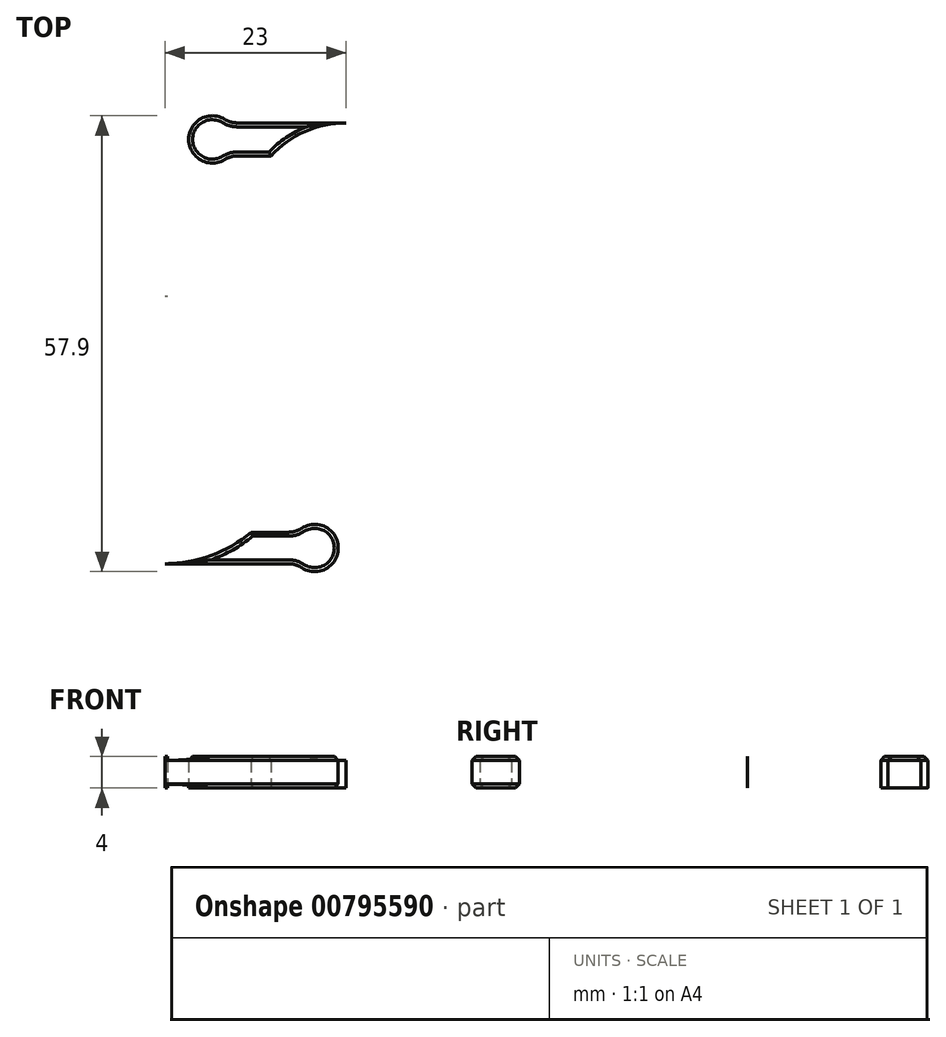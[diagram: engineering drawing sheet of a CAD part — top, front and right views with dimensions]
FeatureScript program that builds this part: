
annotation { "Feature Type Name" : "Feature", "Feature Type Description" : "" }
export const myFeature = defineFeature(function(context is Context, id is Id, definition is map)
    precondition{}
    {
        {
            var Q0;
            Q0=qCreatedBy(makeId("Top.planeOp"),FACE);
            var sketch = newSketch(context, id + "F0", { "sketchPlane" : qUnion([Q0])});
            skCircle(sketch, "E0", {"center": v(0, 0) * mm, "radius": 17 * mm});
            skCircle(sketch, "E1", {"center": v(0, 0) * mm, "radius": 13 * mm});
            skCircle(sketch, "E2", {"center": v(23, 26) * mm, "radius": 13 * mm});
            skCircle(sketch, "E3", {"center": v(23, 25.8) * mm, "radius": 9 * mm});
            skLineSegment(sketch, "E4", {"start": v(0, 17) * mm, "end": v(23, 16.8) * mm});
            skLineSegment(sketch, "E5", {"start": v(0, 13) * mm, "end": v(23, 13) * mm});
            skLineSegment(sketch, "E6", {"start": v(0, -13) * mm, "end": v(19, -13) * mm});
            skLineSegment(sketch, "E7", {"start": v(0, -17) * mm, "end": v(19, -17) * mm});
            skLineSegment(sketch, "E8", {"start": v(23, 39) * mm, "end": v(6, 39) * mm});
            skLineSegment(sketch, "E9", {"start": v(23, 34.8) * mm, "end": v(6, 34.8) * mm});
            skLineSegment(sketch, "E10", {"start": v(6, 39) * mm, "end": v(6, 34.8) * mm});
            skLineSegment(sketch, "E11", {"start": v(19, -13) * mm, "end": v(19, -17) * mm});
            skCircle(sketch, "E12", {"center": v(6, 36.9) * mm, "radius": 3 * mm});
            skCircle(sketch, "E13", {"center": v(19, -15) * mm, "radius": 3 * mm});
            skSolve(sketch);
        }
        {
            var Q0;
            {var subQ0=sQuery(id+"F0.wireOp",EDGE,"E10");Q0=makeQuery(id+"F0.imprint","IMPRINT",FACE,{"disambiguationData":[TD([[makeQuery(id+"F0.imprint","IMPRINT",EDGE,{"derivedFrom":subQ0}),-1.0]])]});}
            var Q1;
            {var subQ5=sQuery(id+"F0.wireOp",EDGE,"E3");var subQ7=makeQuery(id+"F0.imprint","IMPRINT",VERTEX,{"derivedFrom":subQ5});Q1=makeQuery(id+"F0.imprint","IMPRINT",FACE,{"disambiguationData":[TD([[makeQuery(id+"F0.imprint","IMPRINT",EDGE,{"disambiguationData":[TD([[subQ7,1.0]])],"derivedFrom":subQ5}),-1.0]])]});}
            var Q2;
            {var subQ0=sQuery(id+"F0.wireOp",EDGE,"E0");var subQ4=sQuery(id+"F0.wireOp",EDGE,"E4");var subQ6=makeQuery(id+"F0.imprint","INTERSECT",VERTEX,{"disambiguationData":[OD(1.0)],"derivedFrom":[subQ0,subQ4]});Q2=makeQuery(id+"F0.imprint","IMPRINT",FACE,{"disambiguationData":[TD([[makeQuery(id+"F0.imprint","IMPRINT",EDGE,{"disambiguationData":[TD([[subQ6,1.0]])],"derivedFrom":subQ0}),1.0]])]});}
            var Q3;
            {var subQ0=sQuery(id+"F0.wireOp",EDGE,"E8");var subQ1=sQuery(id+"F0.wireOp",EDGE,"E2");var subQ2=makeQuery(id+"F0.imprint","INTERSECT",VERTEX,{"derivedFrom":[subQ1,subQ0]});Q3=makeQuery(id+"F0.imprint","IMPRINT",FACE,{"disambiguationData":[TD([[makeQuery(id+"F0.imprint","IMPRINT",EDGE,{"disambiguationData":[TD([[subQ2,-1.0]])],"derivedFrom":subQ1}),-1.0]])]});}
            var Q4;
            {var subQ0=sQuery(id+"F0.wireOp",EDGE,"E4");var subQ1=sQuery(id+"F0.wireOp",EDGE,"E0");var subQ2=makeQuery(id+"F0.imprint","INTERSECT",VERTEX,{"disambiguationData":[OD(1.0)],"derivedFrom":[subQ1,subQ0]});Q4=makeQuery(id+"F0.imprint","IMPRINT",FACE,{"disambiguationData":[TD([[makeQuery(id+"F0.imprint","IMPRINT",EDGE,{"disambiguationData":[TD([[subQ2,1.0]])],"derivedFrom":subQ1}),-1.0]])]});}
            var Q5;
            {var subQ0=sQuery(id+"F0.wireOp",EDGE,"E7");var subQ1=sQuery(id+"F0.wireOp",EDGE,"E0");var subQ2=makeQuery(id+"F0.imprint","INTERSECT",VERTEX,{"derivedFrom":[subQ1,subQ0]});Q5=makeQuery(id+"F0.imprint","IMPRINT",FACE,{"disambiguationData":[TD([[makeQuery(id+"F0.imprint","IMPRINT",EDGE,{"disambiguationData":[TD([[subQ2,-1.0]])],"derivedFrom":subQ1}),-1.0]])]});}
            var Q6;
            {var subQ0=sQuery(id+"F0.wireOp",EDGE,"E11");Q6=makeQuery(id+"F0.imprint","IMPRINT",FACE,{"disambiguationData":[TD([[makeQuery(id+"F0.imprint","IMPRINT",EDGE,{"derivedFrom":subQ0}),-1.0]])]});}
            var Q7;
            {var subQ0=sQuery(id+"F0.wireOp",EDGE,"E10");Q7=makeQuery(id+"F0.imprint","IMPRINT",FACE,{"disambiguationData":[TD([[makeQuery(id+"F0.imprint","IMPRINT",EDGE,{"derivedFrom":subQ0}),1.0]])]});}
            var Q8;
            {var subQ0=sQuery(id+"F0.wireOp",EDGE,"E11");Q8=makeQuery(id+"F0.imprint","IMPRINT",FACE,{"disambiguationData":[TD([[makeQuery(id+"F0.imprint","IMPRINT",EDGE,{"derivedFrom":subQ0}),1.0]])]});}
            extrude(context, id + "F1", {"entities" : qUnion([Q0, Q1, Q2, Q3, Q4, Q5, Q6, Q7, Q8]), "depth" : 4 * mm, "offsetDistance" : 25 * mm});
        }
        {
            var Q0;
            Q0=makeQuery(id+"F1.opExtrude","SWEPT_EDGE",EDGE,{"disambiguationData":[OSD([sQuery(id+"F0.wireOp",EDGE,"E7"),sQuery(id+"F0.wireOp",EDGE,"E13")])]});
            var Q1;
            Q1=makeQuery(id+"F1.opExtrude","SWEPT_EDGE",EDGE,{"disambiguationData":[OSD([sQuery(id+"F0.wireOp",EDGE,"E9"),sQuery(id+"F0.wireOp",EDGE,"E12")])]});
            var Q2;
            Q2=makeQuery(id+"F1.opExtrude","SWEPT_EDGE",EDGE,{"disambiguationData":[OSD([sQuery(id+"F0.wireOp",EDGE,"E6"),sQuery(id+"F0.wireOp",EDGE,"E13")])]});
            var Q3;
            Q3=makeQuery(id+"F1.opExtrude","SWEPT_EDGE",EDGE,{"disambiguationData":[OSD([sQuery(id+"F0.wireOp",EDGE,"E8"),sQuery(id+"F0.wireOp",EDGE,"E12")])]});
            fillet(context, id + "F2", {"entities" : qUnion([Q0, Q1, Q2, Q3]), "radius" : 3 * mm, "tangentPropagation" : true, "allowEdgeOverflow" : false});
        }
        {
            var Q0;
            Q0=makeQuery(id+"F1.opExtrude","CAP_EDGE",EDGE,{"disambiguationData":[OSD([sQuery(id+"F0.wireOp",EDGE,"E7")])],"isStart":false});
            var Q1;
            Q1=makeQuery(id+"F1.opExtrude","CAP_EDGE",EDGE,{"disambiguationData":[OSD([sQuery(id+"F0.wireOp",EDGE,"E6")])],"isStart":false});
            var Q2;
            Q2=makeQuery(id+"F1.opExtrude","CAP_EDGE",EDGE,{"disambiguationData":[OSD([sQuery(id+"F0.wireOp",EDGE,"E1")])],"isStart":false});
            var Q3;
            Q3=makeQuery(id+"F1.opExtrude","CAP_EDGE",EDGE,{"disambiguationData":[OSD([sQuery(id+"F0.wireOp",EDGE,"E0")])],"isStart":false});
            var Q4;
            Q4=makeQuery(id+"F1.opExtrude","CAP_EDGE",EDGE,{"disambiguationData":[OSD([sQuery(id+"F0.wireOp",EDGE,"E5")])],"isStart":false});
            var Q5;
            Q5=makeQuery(id+"F1.opExtrude","CAP_EDGE",EDGE,{"disambiguationData":[OSD([sQuery(id+"F0.wireOp",EDGE,"E4")])],"isStart":false});
            var Q6;
            Q6=makeQuery(id+"F1.opExtrude","CAP_EDGE",EDGE,{"disambiguationData":[OSD([sQuery(id+"F0.wireOp",EDGE,"E13")])],"isStart":false});
            var Q7;
            {var subQ0=sQuery(id+"F0.wireOp",EDGE,"E13");var subQ1=sQuery(id+"F0.wireOp",EDGE,"E6");Q7=makeQuery(id+"F2.opFillet","BLEND_EDGE",EDGE,{"blendedFrom":[makeQuery(id+"F1.opExtrude","SWEPT_EDGE",EDGE,{"disambiguationData":[OSD([subQ1,subQ0])]}),makeQuery(id+"F1.opExtrude","CAP_FACE",FACE,{"disambiguationData":[OSD([sQuery(id+"F0.wireOp",EDGE,"E0"),sQuery(id+"F0.wireOp",EDGE,"E1"),sQuery(id+"F0.wireOp",EDGE,"E2"),sQuery(id+"F0.wireOp",EDGE,"E3"),sQuery(id+"F0.wireOp",EDGE,"E4"),sQuery(id+"F0.wireOp",EDGE,"E5"),subQ1,sQuery(id+"F0.wireOp",EDGE,"E7"),sQuery(id+"F0.wireOp",EDGE,"E8"),sQuery(id+"F0.wireOp",EDGE,"E9"),sQuery(id+"F0.wireOp",EDGE,"E12"),subQ0])],"isStart":false})],"blendedInto":[makeQuery(id+"F1.opExtrude","CAP_FACE",FACE,{"disambiguationData":[OSD([sQuery(id+"F0.wireOp",EDGE,"E0"),sQuery(id+"F0.wireOp",EDGE,"E1"),sQuery(id+"F0.wireOp",EDGE,"E2"),sQuery(id+"F0.wireOp",EDGE,"E3"),sQuery(id+"F0.wireOp",EDGE,"E4"),sQuery(id+"F0.wireOp",EDGE,"E5"),subQ1,sQuery(id+"F0.wireOp",EDGE,"E7"),sQuery(id+"F0.wireOp",EDGE,"E8"),sQuery(id+"F0.wireOp",EDGE,"E9"),sQuery(id+"F0.wireOp",EDGE,"E12"),subQ0])],"isStart":false})]});}
            var Q8;
            {var subQ0=sQuery(id+"F0.wireOp",EDGE,"E13");var subQ1=sQuery(id+"F0.wireOp",EDGE,"E7");Q8=makeQuery(id+"F2.opFillet","BLEND_EDGE",EDGE,{"blendedFrom":[makeQuery(id+"F1.opExtrude","SWEPT_EDGE",EDGE,{"disambiguationData":[OSD([subQ1,subQ0])]}),makeQuery(id+"F1.opExtrude","CAP_FACE",FACE,{"disambiguationData":[OSD([sQuery(id+"F0.wireOp",EDGE,"E0"),sQuery(id+"F0.wireOp",EDGE,"E1"),sQuery(id+"F0.wireOp",EDGE,"E2"),sQuery(id+"F0.wireOp",EDGE,"E3"),sQuery(id+"F0.wireOp",EDGE,"E4"),sQuery(id+"F0.wireOp",EDGE,"E5"),sQuery(id+"F0.wireOp",EDGE,"E6"),subQ1,sQuery(id+"F0.wireOp",EDGE,"E8"),sQuery(id+"F0.wireOp",EDGE,"E9"),sQuery(id+"F0.wireOp",EDGE,"E12"),subQ0])],"isStart":false})],"blendedInto":[makeQuery(id+"F1.opExtrude","CAP_FACE",FACE,{"disambiguationData":[OSD([sQuery(id+"F0.wireOp",EDGE,"E0"),sQuery(id+"F0.wireOp",EDGE,"E1"),sQuery(id+"F0.wireOp",EDGE,"E2"),sQuery(id+"F0.wireOp",EDGE,"E3"),sQuery(id+"F0.wireOp",EDGE,"E4"),sQuery(id+"F0.wireOp",EDGE,"E5"),sQuery(id+"F0.wireOp",EDGE,"E6"),subQ1,sQuery(id+"F0.wireOp",EDGE,"E8"),sQuery(id+"F0.wireOp",EDGE,"E9"),sQuery(id+"F0.wireOp",EDGE,"E12"),subQ0])],"isStart":false})]});}
            var Q9;
            Q9=makeQuery(id+"F1.opExtrude","CAP_EDGE",EDGE,{"disambiguationData":[OSD([sQuery(id+"F0.wireOp",EDGE,"E2")])],"isStart":false});
            var Q10;
            Q10=makeQuery(id+"F1.opExtrude","CAP_EDGE",EDGE,{"disambiguationData":[OSD([sQuery(id+"F0.wireOp",EDGE,"E3")])],"isStart":false});
            var Q11;
            Q11=makeQuery(id+"F1.opExtrude","CAP_EDGE",EDGE,{"disambiguationData":[OSD([sQuery(id+"F0.wireOp",EDGE,"E9")])],"isStart":false});
            var Q12;
            Q12=makeQuery(id+"F1.opExtrude","CAP_EDGE",EDGE,{"disambiguationData":[OSD([sQuery(id+"F0.wireOp",EDGE,"E8")])],"isStart":false});
            var Q13;
            {var subQ0=sQuery(id+"F0.wireOp",EDGE,"E12");var subQ1=sQuery(id+"F0.wireOp",EDGE,"E9");Q13=makeQuery(id+"F2.opFillet","BLEND_EDGE",EDGE,{"blendedFrom":[makeQuery(id+"F1.opExtrude","SWEPT_EDGE",EDGE,{"disambiguationData":[OSD([subQ1,subQ0])]}),makeQuery(id+"F1.opExtrude","CAP_FACE",FACE,{"disambiguationData":[OSD([sQuery(id+"F0.wireOp",EDGE,"E0"),sQuery(id+"F0.wireOp",EDGE,"E1"),sQuery(id+"F0.wireOp",EDGE,"E2"),sQuery(id+"F0.wireOp",EDGE,"E3"),sQuery(id+"F0.wireOp",EDGE,"E4"),sQuery(id+"F0.wireOp",EDGE,"E5"),sQuery(id+"F0.wireOp",EDGE,"E6"),sQuery(id+"F0.wireOp",EDGE,"E7"),sQuery(id+"F0.wireOp",EDGE,"E8"),subQ1,subQ0,sQuery(id+"F0.wireOp",EDGE,"E13")])],"isStart":false})],"blendedInto":[makeQuery(id+"F1.opExtrude","CAP_FACE",FACE,{"disambiguationData":[OSD([sQuery(id+"F0.wireOp",EDGE,"E0"),sQuery(id+"F0.wireOp",EDGE,"E1"),sQuery(id+"F0.wireOp",EDGE,"E2"),sQuery(id+"F0.wireOp",EDGE,"E3"),sQuery(id+"F0.wireOp",EDGE,"E4"),sQuery(id+"F0.wireOp",EDGE,"E5"),sQuery(id+"F0.wireOp",EDGE,"E6"),sQuery(id+"F0.wireOp",EDGE,"E7"),sQuery(id+"F0.wireOp",EDGE,"E8"),subQ1,subQ0,sQuery(id+"F0.wireOp",EDGE,"E13")])],"isStart":false})]});}
            var Q14;
            {var subQ0=sQuery(id+"F0.wireOp",EDGE,"E12");var subQ1=sQuery(id+"F0.wireOp",EDGE,"E8");Q14=makeQuery(id+"F2.opFillet","BLEND_EDGE",EDGE,{"blendedFrom":[makeQuery(id+"F1.opExtrude","SWEPT_EDGE",EDGE,{"disambiguationData":[OSD([subQ1,subQ0])]}),makeQuery(id+"F1.opExtrude","CAP_FACE",FACE,{"disambiguationData":[OSD([sQuery(id+"F0.wireOp",EDGE,"E0"),sQuery(id+"F0.wireOp",EDGE,"E1"),sQuery(id+"F0.wireOp",EDGE,"E2"),sQuery(id+"F0.wireOp",EDGE,"E3"),sQuery(id+"F0.wireOp",EDGE,"E4"),sQuery(id+"F0.wireOp",EDGE,"E5"),sQuery(id+"F0.wireOp",EDGE,"E6"),sQuery(id+"F0.wireOp",EDGE,"E7"),subQ1,sQuery(id+"F0.wireOp",EDGE,"E9"),subQ0,sQuery(id+"F0.wireOp",EDGE,"E13")])],"isStart":false})],"blendedInto":[makeQuery(id+"F1.opExtrude","CAP_FACE",FACE,{"disambiguationData":[OSD([sQuery(id+"F0.wireOp",EDGE,"E0"),sQuery(id+"F0.wireOp",EDGE,"E1"),sQuery(id+"F0.wireOp",EDGE,"E2"),sQuery(id+"F0.wireOp",EDGE,"E3"),sQuery(id+"F0.wireOp",EDGE,"E4"),sQuery(id+"F0.wireOp",EDGE,"E5"),sQuery(id+"F0.wireOp",EDGE,"E6"),sQuery(id+"F0.wireOp",EDGE,"E7"),subQ1,sQuery(id+"F0.wireOp",EDGE,"E9"),subQ0,sQuery(id+"F0.wireOp",EDGE,"E13")])],"isStart":false})]});}
            var Q15;
            Q15=makeQuery(id+"F1.opExtrude","CAP_EDGE",EDGE,{"disambiguationData":[OSD([sQuery(id+"F0.wireOp",EDGE,"E12")])],"isStart":false});
            var Q16;
            Q16=makeQuery(id+"F1.opExtrude","CAP_EDGE",EDGE,{"disambiguationData":[OSD([sQuery(id+"F0.wireOp",EDGE,"E13")])],"isStart":true});
            var Q17;
            {var subQ0=sQuery(id+"F0.wireOp",EDGE,"E13");var subQ1=sQuery(id+"F0.wireOp",EDGE,"E7");Q17=makeQuery(id+"F2.opFillet","BLEND_EDGE",EDGE,{"blendedFrom":[makeQuery(id+"F1.opExtrude","SWEPT_EDGE",EDGE,{"disambiguationData":[OSD([subQ1,subQ0])]}),makeQuery(id+"F1.opExtrude","CAP_FACE",FACE,{"disambiguationData":[OSD([sQuery(id+"F0.wireOp",EDGE,"E0"),sQuery(id+"F0.wireOp",EDGE,"E1"),sQuery(id+"F0.wireOp",EDGE,"E2"),sQuery(id+"F0.wireOp",EDGE,"E3"),sQuery(id+"F0.wireOp",EDGE,"E4"),sQuery(id+"F0.wireOp",EDGE,"E5"),sQuery(id+"F0.wireOp",EDGE,"E6"),subQ1,sQuery(id+"F0.wireOp",EDGE,"E8"),sQuery(id+"F0.wireOp",EDGE,"E9"),sQuery(id+"F0.wireOp",EDGE,"E12"),subQ0])],"isStart":true})],"blendedInto":[makeQuery(id+"F1.opExtrude","CAP_FACE",FACE,{"disambiguationData":[OSD([sQuery(id+"F0.wireOp",EDGE,"E0"),sQuery(id+"F0.wireOp",EDGE,"E1"),sQuery(id+"F0.wireOp",EDGE,"E2"),sQuery(id+"F0.wireOp",EDGE,"E3"),sQuery(id+"F0.wireOp",EDGE,"E4"),sQuery(id+"F0.wireOp",EDGE,"E5"),sQuery(id+"F0.wireOp",EDGE,"E6"),subQ1,sQuery(id+"F0.wireOp",EDGE,"E8"),sQuery(id+"F0.wireOp",EDGE,"E9"),sQuery(id+"F0.wireOp",EDGE,"E12"),subQ0])],"isStart":true})]});}
            var Q18;
            Q18=makeQuery(id+"F1.opExtrude","CAP_EDGE",EDGE,{"disambiguationData":[OSD([sQuery(id+"F0.wireOp",EDGE,"E6")])],"isStart":true});
            var Q19;
            Q19=makeQuery(id+"F1.opExtrude","CAP_EDGE",EDGE,{"disambiguationData":[OSD([sQuery(id+"F0.wireOp",EDGE,"E7")])],"isStart":true});
            var Q20;
            {var subQ0=sQuery(id+"F0.wireOp",EDGE,"E13");var subQ1=sQuery(id+"F0.wireOp",EDGE,"E6");Q20=makeQuery(id+"F2.opFillet","BLEND_EDGE",EDGE,{"blendedFrom":[makeQuery(id+"F1.opExtrude","SWEPT_EDGE",EDGE,{"disambiguationData":[OSD([subQ1,subQ0])]}),makeQuery(id+"F1.opExtrude","CAP_FACE",FACE,{"disambiguationData":[OSD([sQuery(id+"F0.wireOp",EDGE,"E0"),sQuery(id+"F0.wireOp",EDGE,"E1"),sQuery(id+"F0.wireOp",EDGE,"E2"),sQuery(id+"F0.wireOp",EDGE,"E3"),sQuery(id+"F0.wireOp",EDGE,"E4"),sQuery(id+"F0.wireOp",EDGE,"E5"),subQ1,sQuery(id+"F0.wireOp",EDGE,"E7"),sQuery(id+"F0.wireOp",EDGE,"E8"),sQuery(id+"F0.wireOp",EDGE,"E9"),sQuery(id+"F0.wireOp",EDGE,"E12"),subQ0])],"isStart":true})],"blendedInto":[makeQuery(id+"F1.opExtrude","CAP_FACE",FACE,{"disambiguationData":[OSD([sQuery(id+"F0.wireOp",EDGE,"E0"),sQuery(id+"F0.wireOp",EDGE,"E1"),sQuery(id+"F0.wireOp",EDGE,"E2"),sQuery(id+"F0.wireOp",EDGE,"E3"),sQuery(id+"F0.wireOp",EDGE,"E4"),sQuery(id+"F0.wireOp",EDGE,"E5"),subQ1,sQuery(id+"F0.wireOp",EDGE,"E7"),sQuery(id+"F0.wireOp",EDGE,"E8"),sQuery(id+"F0.wireOp",EDGE,"E9"),sQuery(id+"F0.wireOp",EDGE,"E12"),subQ0])],"isStart":true})]});}
            var Q21;
            Q21=makeQuery(id+"F1.opExtrude","CAP_EDGE",EDGE,{"disambiguationData":[OSD([sQuery(id+"F0.wireOp",EDGE,"E1")])],"isStart":true});
            var Q22;
            Q22=makeQuery(id+"F1.opExtrude","CAP_EDGE",EDGE,{"disambiguationData":[OSD([sQuery(id+"F0.wireOp",EDGE,"E0")])],"isStart":true});
            var Q23;
            Q23=makeQuery(id+"F1.opExtrude","CAP_EDGE",EDGE,{"disambiguationData":[OSD([sQuery(id+"F0.wireOp",EDGE,"E5")])],"isStart":true});
            var Q24;
            Q24=makeQuery(id+"F1.opExtrude","CAP_EDGE",EDGE,{"disambiguationData":[OSD([sQuery(id+"F0.wireOp",EDGE,"E4")])],"isStart":true});
            chamfer(context, id + "F3", {"entities" : qUnion([Q0, Q1, Q2, Q3, Q4, Q5, Q6, Q7, Q8, Q9, Q10, Q11, Q12, Q13, Q14, Q15, Q16, Q17, Q18, Q19, Q20, Q21, Q22, Q23, Q24]), "width" : 0.5 * mm, "tangentPropagation" : true});
        }
    });
